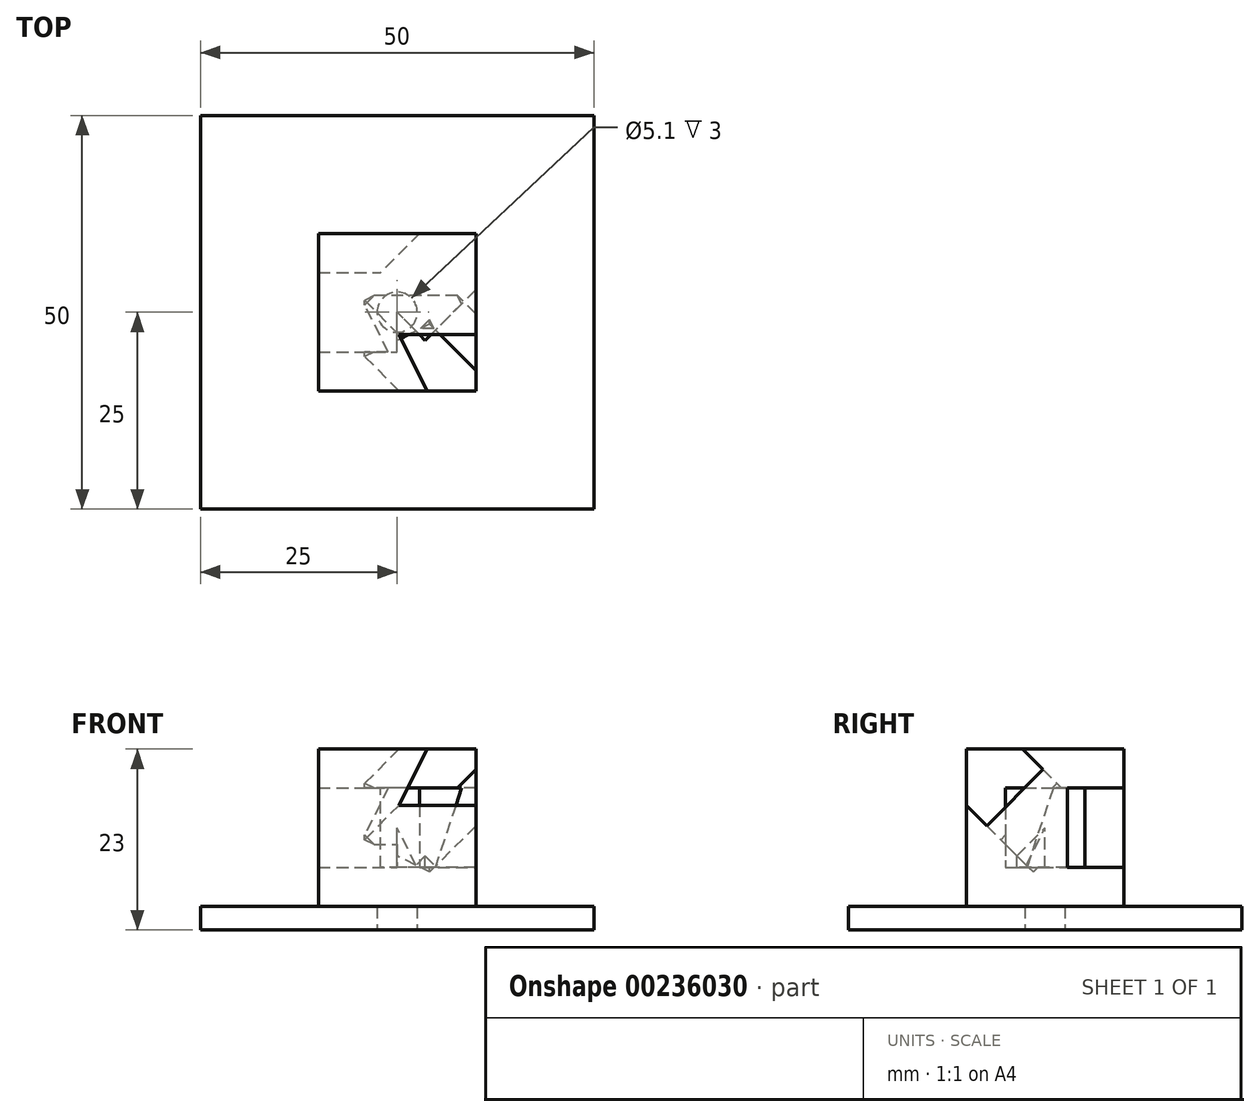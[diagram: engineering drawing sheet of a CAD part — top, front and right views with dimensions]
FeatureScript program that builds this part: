
annotation { "Feature Type Name" : "Feature", "Feature Type Description" : "" }
export const myFeature = defineFeature(function(context is Context, id is Id, definition is map)
    precondition{}
    {
        {
            var Q0;
            Q0=qCreatedBy(makeId("Top.planeOp"),FACE);
            var sketch = newSketch(context, id + "F0", { "sketchPlane" : qUnion([Q0])});
            skLineSegment(sketch, "E0.bottom", {"start": v(-25, 25) * mm, "end": v(25, 25) * mm});
            skLineSegment(sketch, "E0.top", {"start": v(-25, -25) * mm, "end": v(25, -25) * mm});
            skLineSegment(sketch, "E0.left", {"start": v(-25, 25) * mm, "end": v(-25, -25) * mm});
            skLineSegment(sketch, "E0.right", {"start": v(25, 25) * mm, "end": v(25, -25) * mm});
            skPoint(sketch, "E0.middle", {"position": v(0, 0) * mm});
            skCircle(sketch, "E1", {"center": v(0, 0) * mm, "radius": 2.55 * mm});
            skSolve(sketch);
        }
        {
            var Q0;
            Q0 = qSketchRegion(id + "F0", true);
            extrude(context, id + "F1", {"entities" : qUnion([Q0]), "depth" : 3 * mm});
        }
        {
            var Q0;
            Q0=makeQuery(id+"F1.opExtrude","CAP_FACE",FACE,{"disambiguationData":[OSD([sQuery(id+"F0.wireOp",EDGE,"E0.bottom"),sQuery(id+"F0.wireOp",EDGE,"E0.top"),sQuery(id+"F0.wireOp",EDGE,"E0.left"),sQuery(id+"F0.wireOp",EDGE,"E0.right"),sQuery(id+"F0.wireOp",EDGE,"TKBGIfLu-kzoc-njzr-Bxm0-U1IL2JwygMTI.bottom"),sQuery(id+"F0.wireOp",EDGE,"TKBGIfLu-kzoc-njzr-Bxm0-U1IL2JwygMTI.top"),sQuery(id+"F0.wireOp",EDGE,"TKBGIfLu-kzoc-njzr-Bxm0-U1IL2JwygMTI.left"),sQuery(id+"F0.wireOp",EDGE,"TKBGIfLu-kzoc-njzr-Bxm0-U1IL2JwygMTI.right")])],"isStart":false});
            var sketch = newSketch(context, id + "F2", { "sketchPlane" : qUnion([Q0])});
            skLineSegment(sketch, "E2.bottom", {"start": v(-10, 10) * mm, "end": v(10, 10) * mm});
            skLineSegment(sketch, "E2.top", {"start": v(-10, -10) * mm, "end": v(10, -10) * mm});
            skLineSegment(sketch, "E2.left", {"start": v(-10, 10) * mm, "end": v(-10, -10) * mm});
            skLineSegment(sketch, "E2.right", {"start": v(10, 10) * mm, "end": v(10, -10) * mm});
            skPoint(sketch, "E2.middle", {"position": v(0, 0) * mm});
            skSolve(sketch);
        }
        {
            var Q0;
            Q0 = qSketchRegion(id + "F2", true);
            extrude(context, id + "F3", {"entities" : qUnion([Q0]), "operationType" : NewBodyOperationType.ADD, "depth" : 20 * mm});
        }
        {
            var Q0;
            Q0=qCreatedBy(makeId("Right.planeOp"),FACE);
            var sketch = newSketch(context, id + "F4", { "sketchPlane" : qUnion([Q0])});
            skLineSegment(sketch, "E3", {"start": v(0, 23) * mm, "end": v(0, 3) * mm, "construction": true});
            skLineSegment(sketch, "E4.bottom", {"start": v(-5.05, 18.05) * mm, "end": v(5.05, 18.05) * mm});
            skLineSegment(sketch, "E4.top", {"start": v(-5.05, 7.95) * mm, "end": v(5.05, 7.95) * mm});
            skLineSegment(sketch, "E4.left", {"start": v(-5.05, 18.05) * mm, "end": v(-5.05, 7.95) * mm});
            skLineSegment(sketch, "E4.right", {"start": v(5.05, 18.05) * mm, "end": v(5.05, 7.95) * mm});
            skPoint(sketch, "E4.middle", {"position": v(0, 13) * mm});
            skSolve(sketch);
        }
        {
            var Q0;
            Q0 = qSketchRegion(id + "F4", true);
            extrude(context, id + "F5", {"entities" : qUnion([Q0]), "operationType" : NewBodyOperationType.REMOVE, "oppositeDirection" : true, "depth" : 25 * mm});
        }
        {
            var Q0;
            Q0=makeQuery(id+"F3.opExtrude","CAP_VERTEX",VERTEX,{"disambiguationData":[OSD([sQuery(id+"F2.wireOp",EDGE,"E2.bottom"),sQuery(id+"F2.wireOp",EDGE,"E2.left")])],"isStart":false});
            var Q1;
            Q1=makeQuery(id+"F3.opExtrude","CAP_VERTEX",VERTEX,{"disambiguationData":[OSD([sQuery(id+"F2.wireOp",EDGE,"E2.bottom"),sQuery(id+"F2.wireOp",EDGE,"E2.left")])],"isStart":true});
            var Q2;
            Q2=makeQuery(id+"F3.opExtrude","CAP_VERTEX",VERTEX,{"disambiguationData":[OSD([sQuery(id+"F2.wireOp",EDGE,"E2.top"),sQuery(id+"F2.wireOp",EDGE,"E2.right")])],"isStart":false});
            cPlane(context, id + "F6", {"entities" : qUnion([Q0, Q1, Q2]), "cplaneType" : CPlaneType.THREE_POINT, "offset" : 0 * mm, "width" : 150 * mm, "height" : 150 * mm});
        }
        {
            var Q0;
            Q0=qCreatedBy(id+"F6.planeOp",FACE);
            var sketch = newSketch(context, id + "F7", { "sketchPlane" : qUnion([Q0])});
            skLineSegment(sketch, "E5.bottom", {"start": v(-5.05, 7.95) * mm, "end": v(5.05, 7.95) * mm});
            skLineSegment(sketch, "E5.top", {"start": v(-5.05, 18.05) * mm, "end": v(5.05, 18.05) * mm});
            skLineSegment(sketch, "E5.left", {"start": v(-5.05, 7.95) * mm, "end": v(-5.05, 18.05) * mm});
            skLineSegment(sketch, "E5.right", {"start": v(5.05, 7.95) * mm, "end": v(5.05, 18.05) * mm});
            skPoint(sketch, "E5.middle", {"position": v(0, 13) * mm});
            skSolve(sketch);
        }
        {
            var Q0;
            Q0 = qSketchRegion(id + "F7", true);
            extrude(context, id + "F8", {"entities" : qUnion([Q0]), "operationType" : NewBodyOperationType.REMOVE, "depth" : 25 * mm});
        }
        {
            var Q0;
            Q0=makeQuery(id+"F3.opExtrude","CAP_VERTEX",VERTEX,{"disambiguationData":[OSD([sQuery(id+"F2.wireOp",EDGE,"E2.top"),sQuery(id+"F2.wireOp",EDGE,"E2.right")])],"isStart":false});
            var Q1;
            Q1=makeQuery(id+"F3.opExtrude","CAP_VERTEX",VERTEX,{"disambiguationData":[OSD([sQuery(id+"F2.wireOp",EDGE,"E2.bottom"),sQuery(id+"F2.wireOp",EDGE,"E2.left")])],"isStart":true});
            var Q2;
            Q2=makeQuery(id+"F3.opExtrude","CAP_VERTEX",VERTEX,{"disambiguationData":[OSD([sQuery(id+"F2.wireOp",EDGE,"E2.bottom"),sQuery(id+"F2.wireOp",EDGE,"E2.right")])],"isStart":true});
            cPlane(context, id + "F9", {"entities" : qUnion([Q0, Q1, Q2]), "cplaneType" : CPlaneType.THREE_POINT, "offset" : 25 * mm, "width" : 150 * mm, "height" : 150 * mm});
        }
        {
            var Q0;
            Q0=qCreatedBy(id+"F9.planeOp",FACE);
            var sketch = newSketch(context, id + "F10", { "sketchPlane" : qUnion([Q0])});
            skLineSegment(sketch, "E6", {"start": v(-10, 23.33) * mm, "end": v(10, -4.95) * mm, "construction": true});
            skSolve(sketch);
        }
        {
            var Q0;
            Q0=makeQuery(id+"F3.opExtrude","CAP_VERTEX",VERTEX,{"disambiguationData":[OSD([sQuery(id+"F2.wireOp",EDGE,"E2.top"),sQuery(id+"F2.wireOp",EDGE,"E2.left")])],"isStart":true});
            var Q1;
            Q1=makeQuery(id+"F3.opExtrude","CAP_VERTEX",VERTEX,{"disambiguationData":[OSD([sQuery(id+"F2.wireOp",EDGE,"E2.bottom"),sQuery(id+"F2.wireOp",EDGE,"E2.right")])],"isStart":false});
            var Q2;
            Q2=makeQuery(id+"F3.opExtrude","CAP_VERTEX",VERTEX,{"disambiguationData":[OSD([sQuery(id+"F2.wireOp",EDGE,"E2.top"),sQuery(id+"F2.wireOp",EDGE,"E2.right")])],"isStart":true});
            cPlane(context, id + "F11", {"entities" : qUnion([Q0, Q1, Q2]), "cplaneType" : CPlaneType.THREE_POINT, "offset" : 25 * mm, "width" : 150 * mm, "height" : 150 * mm});
        }
        {
            var Q0;
            Q0=qCreatedBy(id+"F11.planeOp",FACE);
            var sketch = newSketch(context, id + "F12", { "sketchPlane" : qUnion([Q0])});
            skLineSegment(sketch, "E7", {"start": v(-10, -4.95) * mm, "end": v(10, 23.33) * mm, "construction": true});
            skSolve(sketch);
        }
        {
            var Q0;
            Q0=sQuery(id+"F12.wireOp",EDGE,"E7");
            cPoint(context, id + "F13", {"entities" : qUnion([Q0]), "parameter" : 0.5});
        }
        {
            var Q0;
            Q0 = qCreatedBy(id + "F13" ,VERTEX);
            var Q1;
            Q1=sQuery(id+"F10.wireOp",EDGE,"E6");
            cPlane(context, id + "F14", {"entities" : qUnion([Q0, Q1]), "cplaneType" : CPlaneType.LINE_POINT, "offset" : 25 * mm, "width" : 150 * mm, "height" : 150 * mm});
        }
        {
            var Q0;
            Q0=qCreatedBy(id+"F14.planeOp",FACE);
            var sketch = newSketch(context, id + "F15", { "sketchPlane" : qUnion([Q0])});
            skLineSegment(sketch, "E8.bottom", {"start": v(0.26, 4.14) * mm, "end": v(10.36, 4.14) * mm});
            skLineSegment(sketch, "E8.top", {"start": v(0.26, 14.24) * mm, "end": v(10.36, 14.24) * mm});
            skLineSegment(sketch, "E8.left", {"start": v(0.26, 4.14) * mm, "end": v(0.26, 14.24) * mm});
            skLineSegment(sketch, "E8.right", {"start": v(10.36, 4.14) * mm, "end": v(10.36, 14.24) * mm});
            skPoint(sketch, "E8.middle", {"position": v(5.3, 9.2) * mm});
            skSolve(sketch);
        }
        {
            var Q0;
            Q0 = qSketchRegion(id + "F15", true);
            extrude(context, id + "F16", {"entities" : qUnion([Q0]), "operationType" : NewBodyOperationType.REMOVE, "oppositeDirection" : true, "depth" : 25 * mm});
        }
    });
